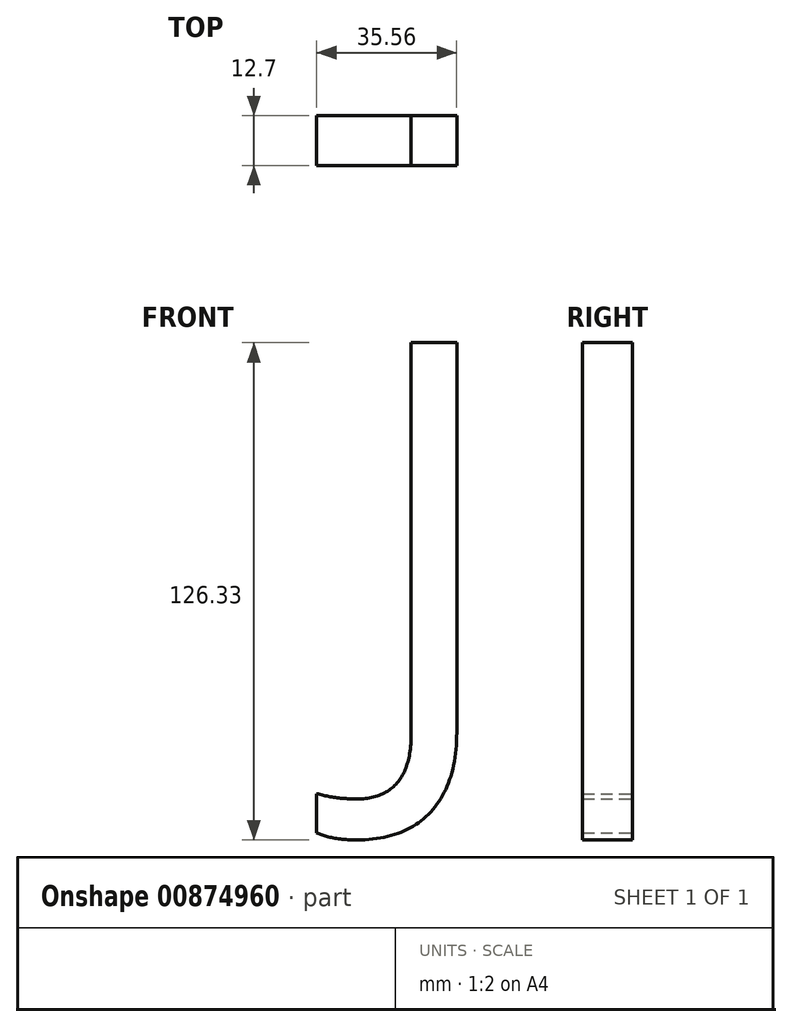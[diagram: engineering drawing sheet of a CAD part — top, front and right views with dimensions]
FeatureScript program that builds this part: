
annotation { "Feature Type Name" : "Feature", "Feature Type Description" : "" }
export const myFeature = defineFeature(function(context is Context, id is Id, definition is map)
    precondition{}
    {
        {
            var Q0;
            Q0=qCreatedBy(makeId("Front.planeOp"),FACE);
            var sketch = newSketch(context, id + "F0", { "sketchPlane" : qUnion([Q0])});
            skText(sketch, "E0", { "text": "J\n", "fontName": "OpenSans-Regular.ttf"});
            const initialGuessF0  = {"E0": [-0.01832, -0.04293, 1, 0, 0.10085]};
            skSetInitialGuess(sketch, initialGuessF0);
            skSolve(sketch);
        }
        {
            var Q0;
            Q0 = qSketchRegion(id + "F0", true);
            extrude(context, id + "F1", {"entities" : qUnion([Q0]), "depth" : 12.7 * mm, "offsetDistance" : 25.4 * mm});
        }
    });
